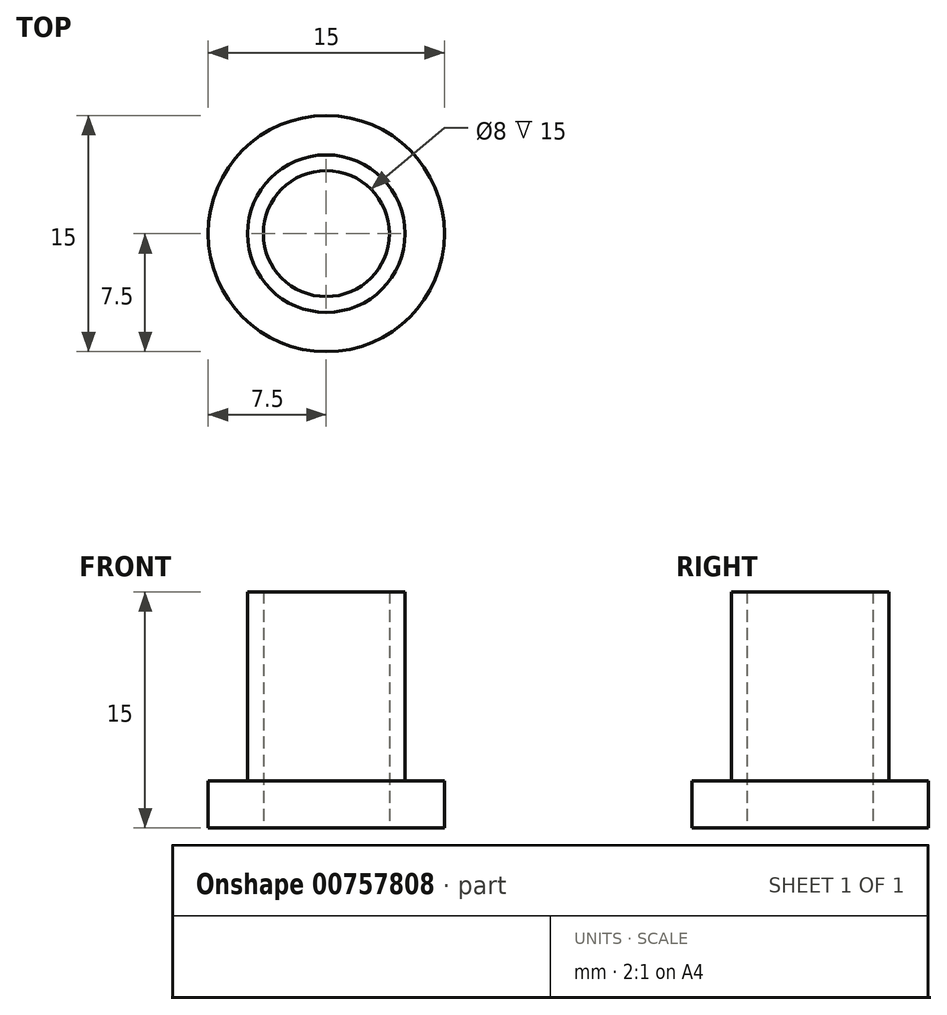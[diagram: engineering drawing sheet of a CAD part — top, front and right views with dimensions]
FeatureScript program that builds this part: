
annotation { "Feature Type Name" : "Feature", "Feature Type Description" : "" }
export const myFeature = defineFeature(function(context is Context, id is Id, definition is map)
    precondition{}
    {
        {
            var Q0;
            Q0=qCreatedBy(makeId("Right.planeOp"),FACE);
            var sketch = newSketch(context, id + "F0", { "sketchPlane" : qUnion([Q0])});
            skLineSegment(sketch, "E0", {"start": v(4, 0) * mm, "end": v(7.5, 0) * mm});
            skLineSegment(sketch, "E1", {"start": v(7.5, 0) * mm, "end": v(7.5, 3) * mm});
            skLineSegment(sketch, "E2", {"start": v(7.5, 3) * mm, "end": v(5, 3) * mm});
            skLineSegment(sketch, "E3", {"start": v(5, 3) * mm, "end": v(5, 15) * mm});
            skLineSegment(sketch, "E4", {"start": v(5, 15) * mm, "end": v(4, 15) * mm});
            skLineSegment(sketch, "E5", {"start": v(4, 15) * mm, "end": v(4, 0) * mm});
            skLineSegment(sketch, "E6", {"start": v(0, 0) * mm, "end": v(0, 38.2) * mm, "construction": true});
            skLineSegment(sketch, "E7", {"start": v(0, 0) * mm, "end": v(4, 0) * mm, "construction": true});
            skSolve(sketch);
        }
        {
            var Q0;
            Q0 = qSketchRegion(id + "F0", true);
            var Q1;
            Q1=sQuery(id+"F0.wireOp",EDGE,"E6");
            revolve(context, id + "F1", {"surfaceOperationType" : NewSurfaceOperationType.NEW, "entities" : qUnion([Q0]), "axis" : qUnion([Q1]), "revolveType" : RevolveType.FULL});
        }
    });
